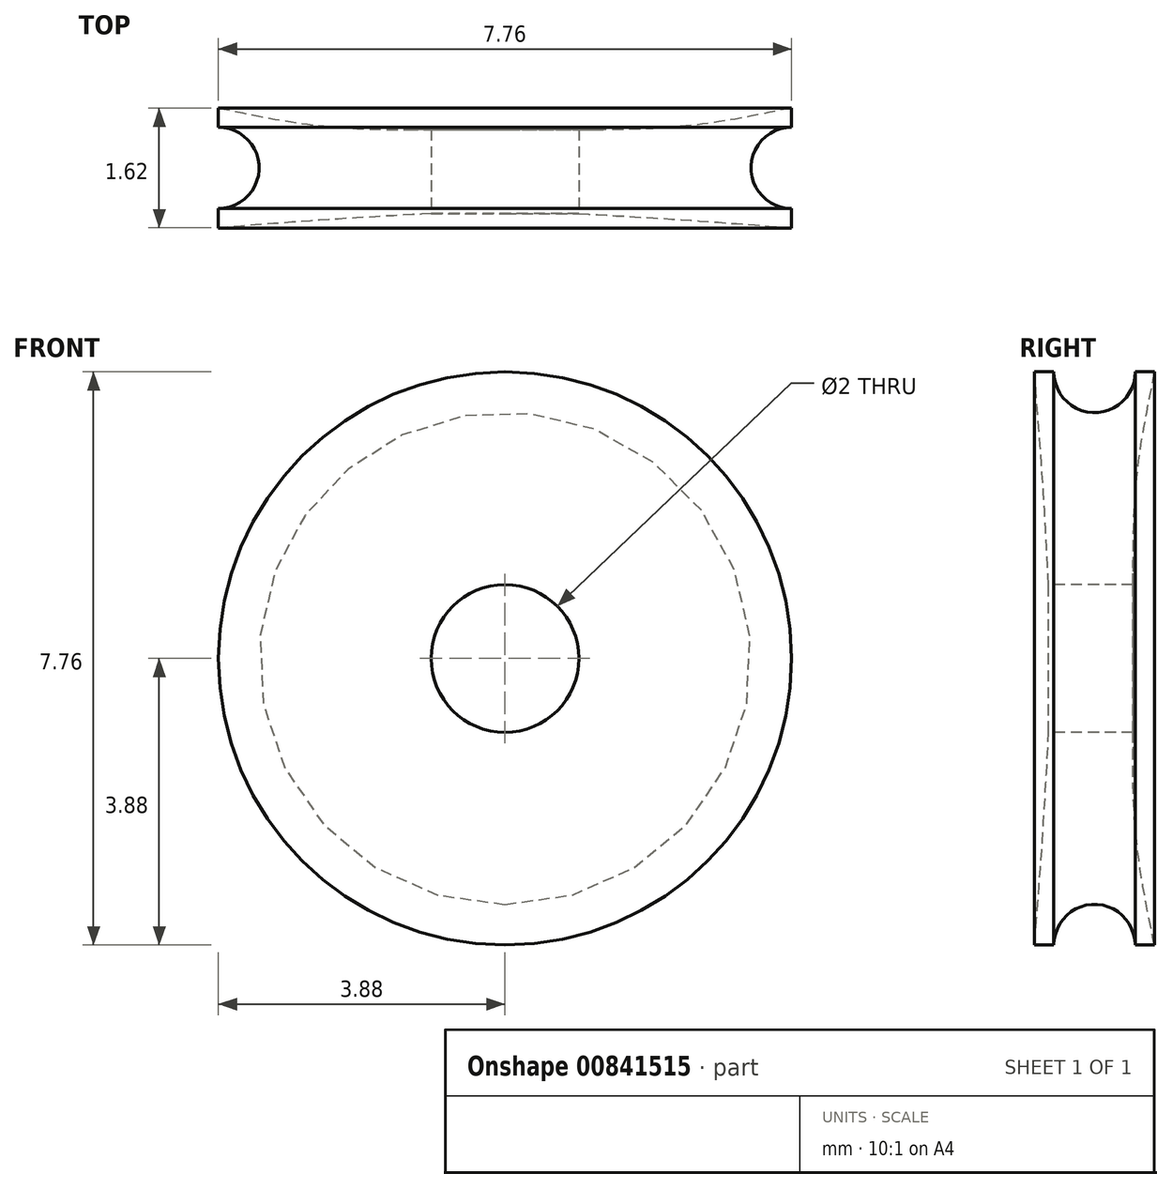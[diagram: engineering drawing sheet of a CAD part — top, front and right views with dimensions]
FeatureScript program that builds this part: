
annotation { "Feature Type Name" : "Feature", "Feature Type Description" : "" }
export const myFeature = defineFeature(function(context is Context, id is Id, definition is map)
    precondition{}
    {
        {
            var Q0;
            Q0=qCreatedBy(makeId("Top.planeOp"),FACE);
            var sketch = newSketch(context, id + "F0", { "sketchPlane" : qUnion([Q0])});
            skArc(sketch, "E0", {"start": v(-3.88, -0.55) * mm, "mid": v(-3.33, 0) * mm, "end": v(-3.88, 0.55) * mm});
            skLineSegment(sketch, "E1", {"start": v(-3.88, -0.55) * mm, "end": v(-3.88, -0.81) * mm});
            skLineSegment(sketch, "E2", {"start": v(-3.88, 0.55) * mm, "end": v(-3.88, 0.81) * mm});
            skLineSegment(sketch, "E3", {"start": v(0, 0) * mm, "end": v(0, 0.55) * mm});
            skLineSegment(sketch, "E4", {"start": v(0, 0) * mm, "end": v(0, -0.57) * mm});
            skLineSegment(sketch, "E5", {"start": v(-3.88, 0) * mm, "end": v(-3.33, 0) * mm});
            skFitSpline(sketch, "E6", {"points": [v(-3.88, 0.81) * mm, v(-2.26, 0.55) * mm, v(0, 0.55) * mm], "startDerivative": vector(3.36, -0.7) * mm, "endDerivative": vector(4.37, 0.15) * mm});
            skFitSpline(sketch, "E7", {"points": [v(-3.88, -0.81) * mm, v(-2.26, -0.7) * mm, v(0, -0.57) * mm], "startDerivative": vector(3.38, 0.27) * mm, "endDerivative": vector(4.35, 0.21) * mm});
            skPoint(sketch, "E8.start.orphan", {"position": v(-2.26, 0) * mm});
            skSolve(sketch);
        }
        {
            var Q0;
            Q0 = qSketchRegion(id + "F0", true);
            var Q1;
            Q1=sQuery(id+"F0.wireOp",EDGE,"E3");
            revolve(context, id + "F1", {"surfaceOperationType" : NewSurfaceOperationType.NEW, "entities" : qUnion([Q0]), "axis" : qUnion([Q1]), "revolveType" : RevolveType.FULL});
        }
        {
            var Q0;
            Q0=qCreatedBy(makeId("Front.planeOp"),FACE);
            var sketch = newSketch(context, id + "F2", { "sketchPlane" : qUnion([Q0])});
            skCircle(sketch, "E9", {"center": v(0, 0) * mm, "radius": 1 * mm});
            skSolve(sketch);
        }
        {
            var Q0;
            Q0 = qSketchRegion(id + "F2", true);
            extrude(context, id + "F3", {"entities" : qUnion([Q0]), "operationType" : NewBodyOperationType.REMOVE, "oppositeDirection" : true, "depth" : 9 * mm, "offsetDistance" : 25 * mm, "hasSecondDirection" : true, "secondDirectionOppositeDirection" : false, "secondDirectionDepth" : 10.2 * mm});
        }
    });
